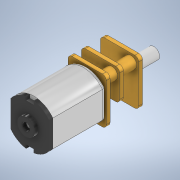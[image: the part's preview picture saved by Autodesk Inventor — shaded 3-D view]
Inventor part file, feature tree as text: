
AUTODESK INVENTOR PART (.ipt)
format: ipt  version: 2022 (Build 260153000, 153)  size: 326,144 bytes
history: native  units: mm
features: extrude x12, sketch x11, projected_geometry x3, fillet x1
ambient origin geometry x8: Origin, YZ Plane, XZ Plane, XY Plane, X Axis, Y Axis, Z Axis, Center Point
bodies: 实体1 (feature_tree), 实体2 (feature_tree), 实体3 (feature_tree)
feature tree (27):
  extrude  "拉伸1"  Depth=2.0mm
  extrude  "拉伸2"  Depth=10.0mm
  extrude  "拉伸3"  Depth=1.0mm
  fillet  "圆角1"  Radius=1.0mm
  extrude  "拉伸4"  Depth=1.0mm TaperAngle=0.0deg
  extrude  "拉伸5"  Depth=1.0mm
  extrude  "拉伸6"  Depth=10.0mm
  extrude  "拉伸7"  Depth=1.0mm TaperAngle=0.0deg
  extrude  "拉伸8"  Depth=2.0mm
  extrude  "拉伸9"  Depth=2.0mm
  sketch  "草图10"  dims[d25=2.0mm d26=2.5mm d27=0.0mm]
  extrude  "拉伸12"  Depth=2.5mm TaperAngle=0.0deg
  extrude  "拉伸10"  Depth=4.0mm TaperAngle=0.0deg
  extrude  "拉伸13"  Depth=1.0mm TaperAngle=0.0deg
  sketch  "草图1"  dims[d0=4.5mm d1=2.0mm]
  sketch  "草图2"  dims[d2=1.0mm d3=0.0mm d4=10.0mm]
  sketch  "草图3"  dims[d7=7.0mm d8=6.0mm d9=1.0mm]
  projected_geometry  "投影回路1"
  sketch  "草图4"  dims[d10=2.0mm d11=1.0mm d12=0.0mm]
  sketch  "草图5"  dims[d13=14.0mm d14=0.0mm d15=1.0mm]
  sketch  "草图6"  dims[d16=1.0mm d17=10.0mm]
  projected_geometry  "投影回路2"
  sketch  "草图7"  dims[d18=12.0mm d19=1.0mm d20=0.0mm]
  sketch  "草图8"  dims[d21=3.0mm d22=2.0mm]
  projected_geometry  "投影回路3"
  sketch  "草图9"  dims[d23=2.0mm d24=2.0mm]
  sketch  "草图11"  dims[d28=1.0mm d29=0.0mm d30=4.0mm d31=0.0mm d32=1.0mm d33=0.0mm d34=4.0mm d35=3.0mm d36=0.5mm d37=0.0mm d38=2.3mm d39=3.0mm d40=0.6mm d41=0.0mm d45=4.0mm d46=1.0mm d47=1.0mm d48=1.5mm d49=0.0mm d50=8.0mm d51=0.0mm]
